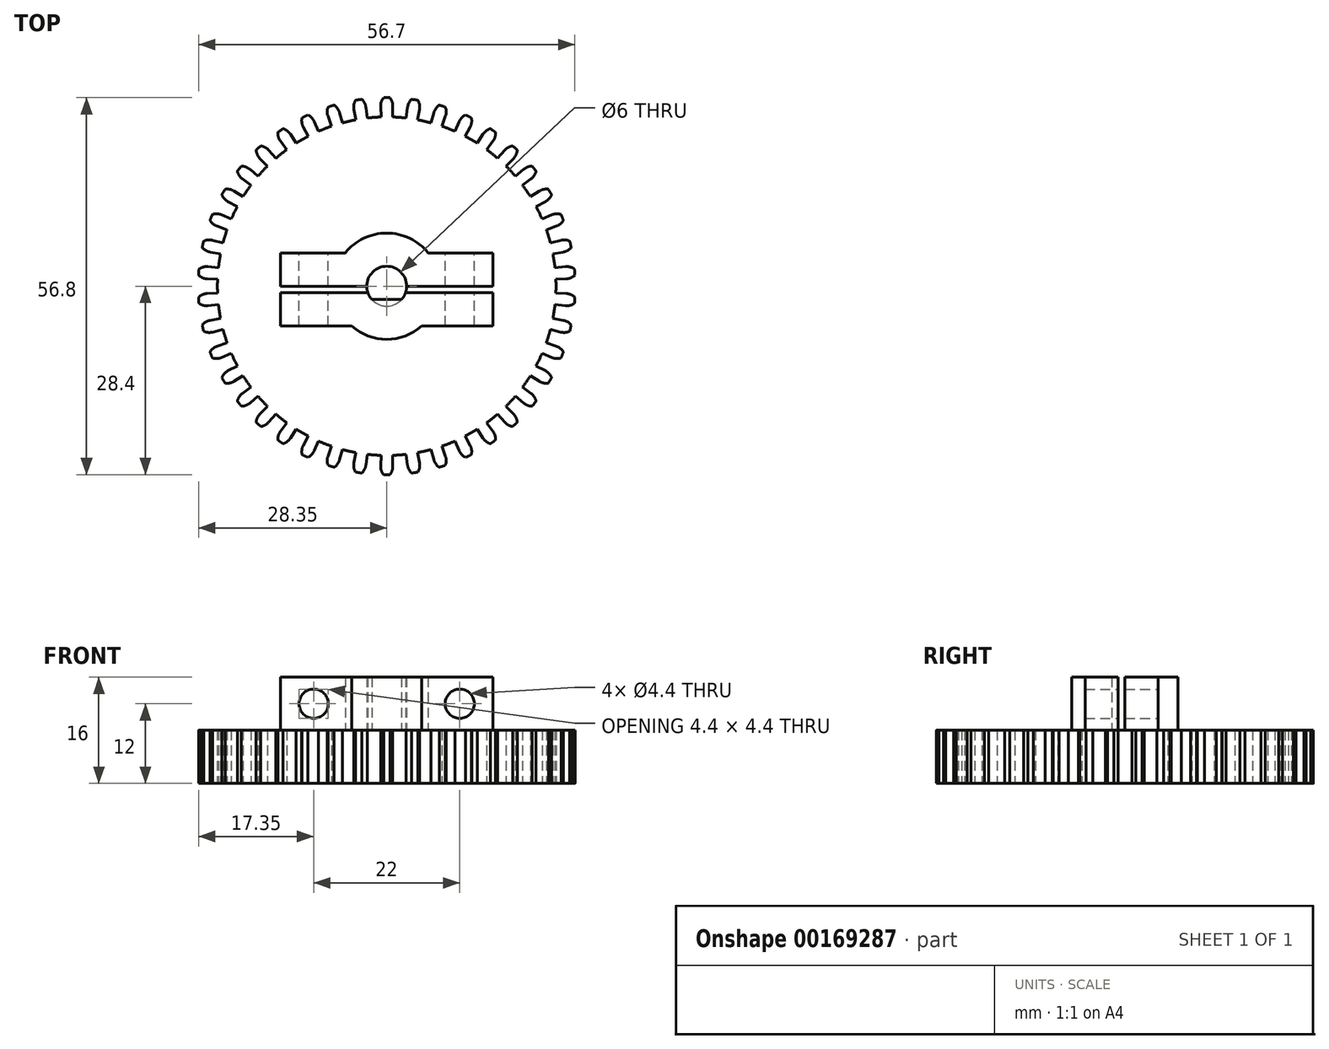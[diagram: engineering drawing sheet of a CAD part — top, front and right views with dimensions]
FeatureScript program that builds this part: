
annotation { "Feature Type Name" : "Feature", "Feature Type Description" : "" }
export const myFeature = defineFeature(function(context is Context, id is Id, definition is map)
    precondition{}
    {
        {
            var Q0;
            Q0=qCreatedBy(makeId("Top.planeOp"),FACE);
            var sketch = newSketch(context, id + "F0", { "sketchPlane" : qUnion([Q0])});
            skCircle(sketch, "E0", {"center": v(0, 0) * mm, "radius": 28.4 * mm});
            skCircle(sketch, "E1", {"center": v(0, 0) * mm, "radius": 3 * mm});
            skCircle(sketch, "E2", {"center": v(0, 0) * mm, "radius": 25.5 * mm});
            skCircle(sketch, "E3", {"center": v(0, 0) * mm, "radius": 27.1 * mm, "construction": true});
            skLineSegment(sketch, "E4", {"start": v(0, 0) * mm, "end": v(0, 39.28) * mm, "construction": true});
            skLineSegment(sketch, "E5", {"start": v(0, 0) * mm, "end": v(0.59, 34.86) * mm, "construction": true});
            skLineSegment(sketch, "E6", {"start": v(0, 0) * mm, "end": v(0.87, 25.96) * mm, "construction": true});
            skLineSegment(sketch, "E7", {"start": v(0, 0) * mm, "end": v(2.96, 39.48) * mm, "construction": true});
            skArc(sketch, "E8", {"start": v(0.91, 27.08) * mm, "mid": v(0.81, 27.78) * mm, "end": v(0.48, 28.4) * mm});
            skLineSegment(sketch, "E9", {"start": v(0.91, 27.08) * mm, "end": v(0.86, 25.49) * mm});
            skArc(sketch, "E10", {"start": v(0, 28.4) * mm, "mid": v(0.24, 28.4) * mm, "end": v(0.48, 28.4) * mm});
            skArc(sketch, "E11", {"start": v(0.86, 25.49) * mm, "mid": v(1.38, 25.46) * mm, "end": v(1.9, 25.43) * mm});
            skArc(sketch, "E12.MirrorCS", {"start": v(0, 28.4) * mm, "mid": v(-0.24, 28.4) * mm, "end": v(-0.48, 28.4) * mm});
            skArc(sketch, "E13.MirrorCS", {"start": v(-0.91, 27.08) * mm, "mid": v(-0.81, 27.78) * mm, "end": v(-0.48, 28.4) * mm});
            skLineSegment(sketch, "E14.MirrorCS", {"start": v(-0.91, 27.08) * mm, "end": v(-0.86, 25.49) * mm});
            skArc(sketch, "E15.MirrorCS", {"start": v(-0.86, 25.49) * mm, "mid": v(-1.38, 25.46) * mm, "end": v(-1.9, 25.43) * mm});
            skSolve(sketch);
        }
        {
            var Q0;
            Q0=makeQuery(id+"F0.imprint","IMPRINT",FACE,{"disambiguationData":[TD([[makeQuery(id+"F0.imprint","IMPRINT",EDGE,{"derivedFrom":sQuery(id+"F0.wireOp",EDGE,"E1")}),-1.0]])]});
            var Q1;
            {var subQ1=sQuery(id+"F0.wireOp",EDGE,"E8");Q1=makeQuery(id+"F0.imprint","IMPRINT",FACE,{"disambiguationData":[TD([[makeQuery(id+"F0.imprint","IMPRINT",EDGE,{"derivedFrom":subQ1}),1.0]])]});}
            extrude(context, id + "F1", {"entities" : qUnion([Q0, Q1]), "depth" : 8 * mm});
        }
        {
            var Q0;
            Q0=makeQuery(id+"F1.opExtrude","SWEPT_BODY",BODY,{"disambiguationData":[OSD([sQuery(id+"F0.wireOp",EDGE,"E0"),sQuery(id+"F0.wireOp",EDGE,"E1"),sQuery(id+"F0.wireOp",EDGE,"E2"),sQuery(id+"F0.wireOp",EDGE,"E8"),sQuery(id+"F0.wireOp",EDGE,"E9"),sQuery(id+"F0.wireOp",EDGE,"E13.MirrorCS"),sQuery(id+"F0.wireOp",EDGE,"E14.MirrorCS")])]});
            var Q1;
            Q1=makeQuery(id+"F1.opExtrude","SWEPT_FACE",FACE,{"disambiguationData":[OSD([sQuery(id+"F0.wireOp",EDGE,"E1")])]});
            circularPattern(context, id + "F2", {"operationType" : NewBodyOperationType.ADD, "entities" : qUnion([Q0]), "axis" : qUnion([Q1]), "angle" : 8.57 * degree, "instanceCount" : 42});
        }
        {
            var Q0;
            Q0=makeQuery(id+"F1.opExtrude","CAP_FACE",FACE,{"disambiguationData":[OSD([sQuery(id+"F0.wireOp",EDGE,"E0"),sQuery(id+"F0.wireOp",EDGE,"E1")])],"isStart":false});
            var sketch = newSketch(context, id + "F3", { "sketchPlane" : qUnion([Q0])});
            skCircle(sketch, "E16", {"center": v(0, 0) * mm, "radius": 3 * mm});
            skCircle(sketch, "E17", {"center": v(0, 0) * mm, "radius": 8 * mm});
            skLineSegment(sketch, "E18", {"start": v(-3, 0) * mm, "end": v(-16, 0) * mm});
            skLineSegment(sketch, "E19", {"start": v(-16, 0) * mm, "end": v(-16, 5) * mm});
            skLineSegment(sketch, "E20", {"start": v(-16, 5) * mm, "end": v(-6.24, 5) * mm});
            skLineSegment(sketch, "E21", {"start": v(0, 12.07) * mm, "end": v(0, -18.27) * mm, "construction": true});
            skLineSegment(sketch, "E22.MirrorCS", {"start": v(16, 0) * mm, "end": v(16, 5) * mm});
            skLineSegment(sketch, "E23.MirrorCS", {"start": v(3, 0) * mm, "end": v(16, 0) * mm});
            skLineSegment(sketch, "E24.MirrorCS", {"start": v(16, 5) * mm, "end": v(6.24, 5) * mm});
            skLineSegment(sketch, "E25", {"start": v(-2.83, -1) * mm, "end": v(-16, -1) * mm});
            skLineSegment(sketch, "E26", {"start": v(-16, -1) * mm, "end": v(-16, -6) * mm});
            skLineSegment(sketch, "E27", {"start": v(-16, -6) * mm, "end": v(-5.3, -6) * mm});
            skLineSegment(sketch, "E28", {"start": v(-2.24, -2) * mm, "end": v(2.24, -2) * mm});
            skLineSegment(sketch, "E29.MirrorCS", {"start": v(16, -6) * mm, "end": v(5.3, -6) * mm});
            skLineSegment(sketch, "E30.MirrorCS", {"start": v(16, -1) * mm, "end": v(16, -6) * mm});
            skLineSegment(sketch, "E31.MirrorCS", {"start": v(2.83, -1) * mm, "end": v(16, -1) * mm});
            skSolve(sketch);
        }
        {
            var Q0;
            {var subQ4=sQuery(id+"F3.wireOp",EDGE,"E19");Q0=makeQuery(id+"F3.imprint","IMPRINT",FACE,{"disambiguationData":[TD([[makeQuery(id+"F3.imprint","IMPRINT",EDGE,{"derivedFrom":subQ4}),-1.0]])]});}
            var Q1;
            {var subQ2=sQuery(id+"F3.wireOp",EDGE,"E18");var subQ7=sQuery(id+"F3.wireOp",EDGE,"E16");var subQ8=makeQuery(id+"F3.imprint","INTERSECT",VERTEX,{"derivedFrom":[subQ7,subQ2]});Q1=makeQuery(id+"F3.imprint","IMPRINT",FACE,{"disambiguationData":[TD([[makeQuery(id+"F3.imprint","IMPRINT",EDGE,{"disambiguationData":[TD([[subQ8,1.0]])],"derivedFrom":subQ7}),-1.0]])]});}
            var Q2;
            {var subQ4=sQuery(id+"F3.wireOp",EDGE,"E22.MirrorCS");Q2=makeQuery(id+"F3.imprint","IMPRINT",FACE,{"disambiguationData":[TD([[makeQuery(id+"F3.imprint","IMPRINT",EDGE,{"derivedFrom":subQ4}),1.0]])]});}
            extrude(context, id + "F4", {"entities" : qUnion([Q0, Q1, Q2]), "operationType" : NewBodyOperationType.ADD, "depth" : 8 * mm});
        }
        {
            var Q0;
            Q0=makeQuery(id+"F4.opExtrude","SWEPT_FACE",FACE,{"disambiguationData":[OSD([sQuery(id+"F3.wireOp",EDGE,"E24.MirrorCS")])]});
            var sketch = newSketch(context, id + "F5", { "sketchPlane" : qUnion([Q0])});
            skPoint(sketch, "E32", {"position": v(-11, 12) * mm});
            skPoint(sketch, "E33", {"position": v(11, 12) * mm});
            skSolve(sketch);
        }
        {
            var Q0;
            {var subQ4=sQuery(id+"F3.wireOp",EDGE,"E26");Q0=makeQuery(id+"F3.imprint","IMPRINT",FACE,{"disambiguationData":[TD([[makeQuery(id+"F3.imprint","IMPRINT",EDGE,{"derivedFrom":subQ4}),1.0]])]});}
            var Q1;
            {var subQ1=sQuery(id+"F3.wireOp",EDGE,"E16");var subQ7=sQuery(id+"F3.wireOp",EDGE,"E25");var subQ10=makeQuery(id+"F3.imprint","INTERSECT",VERTEX,{"derivedFrom":[subQ1,subQ7]});Q1=makeQuery(id+"F3.imprint","IMPRINT",FACE,{"disambiguationData":[TD([[makeQuery(id+"F3.imprint","IMPRINT",EDGE,{"disambiguationData":[TD([[subQ10,-1.0]])],"derivedFrom":subQ1}),-1.0]])]});}
            var Q2;
            {var subQ0=sQuery(id+"F3.wireOp",EDGE,"E29.MirrorCS");Q2=makeQuery(id+"F3.imprint","IMPRINT",FACE,{"disambiguationData":[TD([[makeQuery(id+"F3.imprint","IMPRINT",EDGE,{"derivedFrom":subQ0}),-1.0]])]});}
            var Q3;
            {var subQ0=sQuery(id+"F3.wireOp",EDGE,"E28");Q3=makeQuery(id+"F3.imprint","IMPRINT",FACE,{"disambiguationData":[TD([[makeQuery(id+"F3.imprint","IMPRINT",EDGE,{"derivedFrom":subQ0}),-1.0]])]});}
            extrude(context, id + "F6", {"entities" : qUnion([Q0, Q1, Q2, Q3]), "depth" : 8 * mm});
        }
        {
            var Q0;
            Q0=sQuery(id+"F5.wireOp",VERTEX,"E32");
            var Q1;
            Q1=sQuery(id+"F5.wireOp",VERTEX,"E33");
            var Q2;
            Q2=makeQuery(id+"F6.opExtrude","SWEPT_BODY",BODY,{"disambiguationData":[OSD([sQuery(id+"F3.wireOp",EDGE,"E16"),sQuery(id+"F3.wireOp",EDGE,"E17"),sQuery(id+"F3.wireOp",EDGE,"E25"),sQuery(id+"F3.wireOp",EDGE,"E26"),sQuery(id+"F3.wireOp",EDGE,"E27"),sQuery(id+"F3.wireOp",EDGE,"E28"),sQuery(id+"F3.wireOp",EDGE,"E29.MirrorCS"),sQuery(id+"F3.wireOp",EDGE,"E30.MirrorCS"),sQuery(id+"F3.wireOp",EDGE,"E31.MirrorCS")])]});
            var Q3;
            Q3=makeQuery(id+"F1.opExtrude","SWEPT_BODY",BODY,{"disambiguationData":[OSD([sQuery(id+"F0.wireOp",EDGE,"E0"),sQuery(id+"F0.wireOp",EDGE,"E1")])]});
            hole(context, id + "F7", {"style" : HoleStyle.SIMPLE, "endStyle" : HoleEndStyle.THROUGH, "standardTappedOrClearance" : lookupTablePath({ "standard" : "ISO", "fit" : "Normal", "size" : "M4", "type" : "Clearance" }), "standardBlindInLast" : lookupTablePath({ "fit" : "Standard", "standard" : "ISO", "size" : "M4", "type" : "Clearance" }), "holeDiameter" : 4.4 * mm, "locations" : qUnion([Q0, Q1]), "scope" : qUnion([Q2, Q3]), "isTappedThrough" : true});
        }
    });
